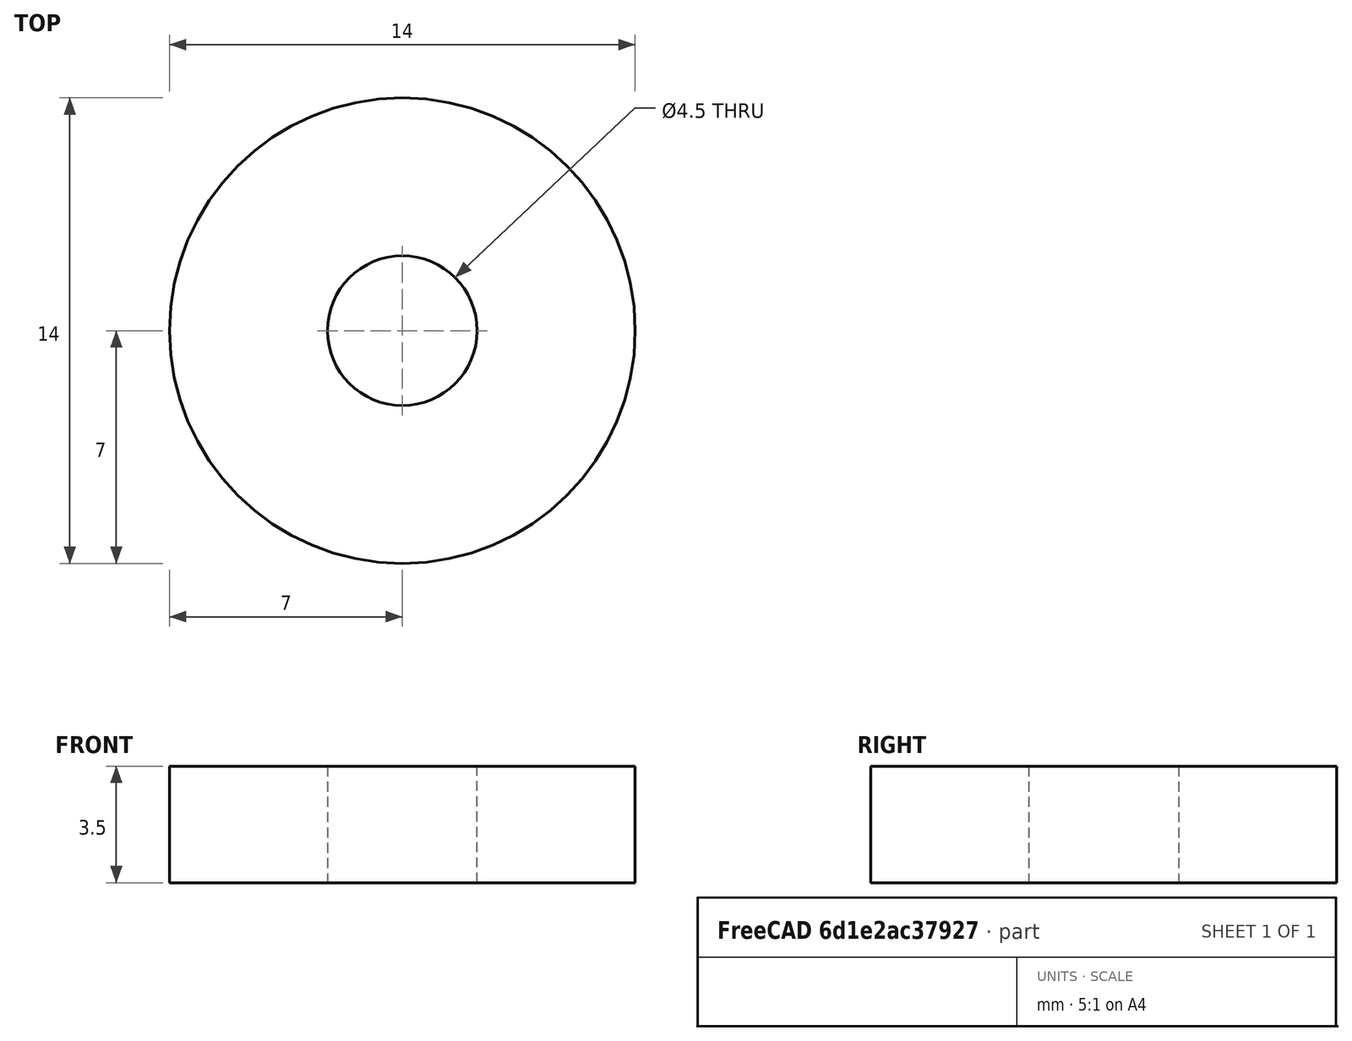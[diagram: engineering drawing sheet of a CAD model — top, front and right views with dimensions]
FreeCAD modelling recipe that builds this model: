
FCSTD DOCUMENT  (FreeCAD 1.0R38641 +468 (Git))
Label: Roller
License: All rights reserved
LicenseURL: https://en.wikipedia.org/wiki/All_rights_reserved
objects: Sketcher::SketchObject×1, PartDesign::Pad×1, PartDesign::Body×1
note: 6 computed .brp shape members not serialized (recipe doc carries the construction recipe); baked Part::Feature solids carry a one-line shape summary decoded from their .brp

FEATURE [Sketcher::SketchObject] Sketch
  ArcFitTolerance = 1e-06
  AttachmentSupport = -> [XY_Plane]
  FullyConstrained = true
  MakeInternals = false
  MapMode = 5
  sketch-geometry (2):
    g0: Circle CenterX=0 CenterY=0 CenterZ=0 NormalX=0 NormalY=0 NormalZ=1 AngleXU=0 Radius=7
    g1: Circle CenterX=0 CenterY=0 CenterZ=0 NormalX=0 NormalY=0 NormalZ=1 AngleXU=0 Radius=2.25
  constraints (4):
    c: Diameter(g0) = 14
    c: Coincident(g0,g-1)
    c: Diameter(g1) = 4.5
    c: Coincident(g1,g0)
FEATURE [PartDesign::Pad] Pad
  Direction = (0,0,1)
  Length = 3.5
  Length2 = 10
  Profile = -> Sketch
  ReferenceAxis = -> Sketch [N_Axis]
  Refine = true
  Suppressed = false
  Type = 0
FEATURE [PartDesign::Body] Body
  AllowCompound = false
  Group = -> [Sketch,Pad]
  Origin = -> Origin
  Tip = -> Pad
